# Revit family: Gira_511000
name_source: partatom
category: Elektroinstallationen
revit_build: Autodesk Revit 2017 (Build: 20160225_1515(x64)
units: mm (PartAtom-declared; Revit-internal decimal feet)

## family parameters
Basisbauteil = Fläche
Beim Laden mit Abzugskörper schneiden = Nein
Bemaßung runder Anschluss = Durchmesser verwenden
Beschriftungsausrichtung beibehalten = Nein
Gemeinsam genutzt = Nein
Raumberechnungspunkt = Nein
Teiletyp = Normal

## types (1)
- Gira_511000
    Art des Zubehörs = sonstige
    BIM = https://media.stage.bim.site
    Beschreibung = KNX RF TP Medienkoppler oder RF Repeater  REG plus Mit den KNX RF Systemgeräten werden die KNX RF Tastsensoren und KNX RF Handsender über die ETS in die KNX Struktur eingebunden und parametriert.  Merkmale: - Schnittstelle zwischen verdrahteten KNX Produkten (TP) und KNX RF Funkprodukten. - Über die ETS als Medienkoppler oder Repeater konfigurierbar. - Projektierung, Inbetriebnahme und Parametrierung erfolgen über ETS (Version 5 oder neuer).
    Datenblatt = https://katalog.gira.de
    GTIN = 4010337017264
    HAN = 511000
    Hersteller = Gira
    Produktseite = http://katalog.gira.de
    Typname = RF/TP Medienkoppler/RF Repeater KNX
    URL = https://www.gira.de
    Vorgabe-Ansicht = 1219 mm

## geometry (parser evidence)
native form markers: Sweep x2
no freeform markers — native parametric forms only
